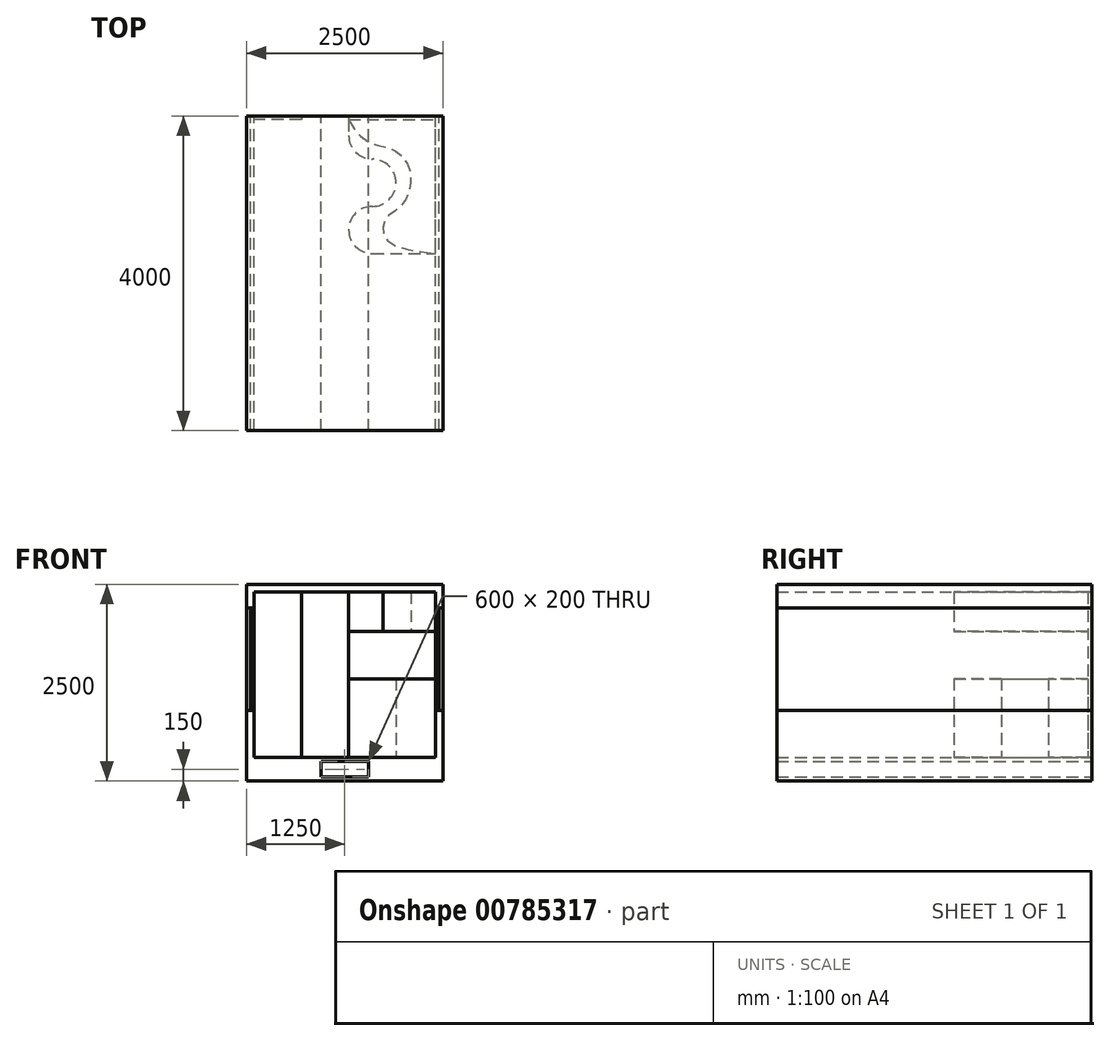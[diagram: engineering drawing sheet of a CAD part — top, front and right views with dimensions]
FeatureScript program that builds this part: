
annotation { "Feature Type Name" : "Feature", "Feature Type Description" : "" }
export const myFeature = defineFeature(function(context is Context, id is Id, definition is map)
    precondition{}
    {
        {
            var Q0;
            Q0=qCreatedBy(makeId("Front.planeOp"),FACE);
            var sketch = newSketch(context, id + "F0", { "sketchPlane" : qUnion([Q0])});
            skLineSegment(sketch, "E0", {"start": v(0, 0) * mm, "end": v(1250, 0) * mm});
            skLineSegment(sketch, "E1", {"start": v(0, 0) * mm, "end": v(-1250, 0) * mm});
            skLineSegment(sketch, "E2", {"start": v(-1250, 0) * mm, "end": v(-1250, 900) * mm});
            skLineSegment(sketch, "E3", {"start": v(-1250, 900) * mm, "end": v(-1150, 900) * mm});
            skLineSegment(sketch, "E4", {"start": v(-1150, 900) * mm, "end": v(-1150, 50) * mm});
            skLineSegment(sketch, "E5", {"start": v(-1150, 50) * mm, "end": v(1150, 50) * mm});
            skLineSegment(sketch, "E6", {"start": v(1150, 50) * mm, "end": v(1150, 900) * mm});
            skLineSegment(sketch, "E7", {"start": v(1150, 900) * mm, "end": v(1250, 900) * mm});
            skLineSegment(sketch, "E8", {"start": v(1250, 900) * mm, "end": v(1250, 0) * mm});
            skLineSegment(sketch, "E9", {"start": v(-1250, 900) * mm, "end": v(-1250, 2200) * mm});
            skLineSegment(sketch, "E10", {"start": v(-1250, 2200) * mm, "end": v(-1250, 2500) * mm});
            skLineSegment(sketch, "E11", {"start": v(-1250, 2500) * mm, "end": v(1250, 2500) * mm});
            skLineSegment(sketch, "E12", {"start": v(1250, 2500) * mm, "end": v(1250, 2200) * mm});
            skLineSegment(sketch, "E13", {"start": v(1250, 2200) * mm, "end": v(1250, 900) * mm});
            skLineSegment(sketch, "E14", {"start": v(-1250, 2200) * mm, "end": v(-1150, 2200) * mm});
            skLineSegment(sketch, "E15", {"start": v(-1150, 2200) * mm, "end": v(-1150, 2400) * mm});
            skLineSegment(sketch, "E16", {"start": v(-1150, 2400) * mm, "end": v(1150, 2400) * mm});
            skLineSegment(sketch, "E17", {"start": v(1150, 2400) * mm, "end": v(1150, 2200) * mm});
            skLineSegment(sketch, "E18", {"start": v(1150, 2200) * mm, "end": v(1250, 2200) * mm});
            skLineSegment(sketch, "E19", {"start": v(-1200, 900) * mm, "end": v(-1200, 2200) * mm});
            skLineSegment(sketch, "E20", {"start": v(1200, 2200) * mm, "end": v(1200, 900) * mm});
            skPoint(sketch, "E21", {"position": v(-1150, 250) * mm});
            skLineSegment(sketch, "E22", {"start": v(-1150, 250) * mm, "end": v(-300, 250) * mm});
            skLineSegment(sketch, "E23", {"start": v(-300, 250) * mm, "end": v(-300, 50) * mm});
            skLineSegment(sketch, "E24", {"start": v(1150, 250) * mm, "end": v(300, 250) * mm});
            skLineSegment(sketch, "E25", {"start": v(300, 250) * mm, "end": v(300, 50) * mm});
            skLineSegment(sketch, "E26", {"start": v(-300, 250) * mm, "end": v(300, 250) * mm});
            skLineSegment(sketch, "E27", {"start": v(-1150, 324) * mm, "end": v(1150, 324) * mm});
            skSolve(sketch);
        }
        {
            var Q0;
            Q0=makeQuery(id+"F0.imprint","IMPRINT",FACE,{"disambiguationData":[TD([[makeQuery(id+"F0.imprint","IMPRINT",EDGE,{"derivedFrom":sQuery(id+"F0.wireOp",EDGE,"E0")}),1.0]])]});
            var Q1;
            {var subQ4=sQuery(id+"F0.wireOp",EDGE,"E24");Q1=makeQuery(id+"F0.imprint","IMPRINT",FACE,{"disambiguationData":[TD([[makeQuery(id+"F0.imprint","IMPRINT",EDGE,{"derivedFrom":subQ4}),1.0]])]});}
            var Q2;
            {var subQ3=sQuery(id+"F0.wireOp",EDGE,"E22");Q2=makeQuery(id+"F0.imprint","IMPRINT",FACE,{"disambiguationData":[TD([[makeQuery(id+"F0.imprint","IMPRINT",EDGE,{"derivedFrom":subQ3}),-1.0]])]});}
            var Q3;
            {var subQ3=sQuery(id+"F0.wireOp",EDGE,"E22");Q3=makeQuery(id+"F0.imprint","IMPRINT",FACE,{"disambiguationData":[TD([[makeQuery(id+"F0.imprint","IMPRINT",EDGE,{"derivedFrom":subQ3}),1.0]])]});}
            var Q4;
            {var subQ1=sQuery(id+"F0.wireOp",EDGE,"E10");Q4=makeQuery(id+"F0.imprint","IMPRINT",FACE,{"disambiguationData":[TD([[makeQuery(id+"F0.imprint","IMPRINT",EDGE,{"derivedFrom":subQ1}),-1.0]])]});}
            extrude(context, id + "F1", {"entities" : qUnion([Q0, Q1, Q2, Q3, Q4]), "depth" : 4000 * mm, "offsetDistance" : 25 * mm});
        }
        {
            var Q0;
            {var subQ0=sQuery(id+"F0.wireOp",EDGE,"E9");Q0=makeQuery(id+"F0.imprint","IMPRINT",FACE,{"disambiguationData":[TD([[makeQuery(id+"F0.imprint","IMPRINT",EDGE,{"derivedFrom":subQ0}),-1.0]])]});}
            var Q1;
            {var subQ0=sQuery(id+"F0.wireOp",EDGE,"E13");Q1=makeQuery(id+"F0.imprint","IMPRINT",FACE,{"disambiguationData":[TD([[makeQuery(id+"F0.imprint","IMPRINT",EDGE,{"derivedFrom":subQ0}),-1.0]])]});}
            extrude(context, id + "F2", {"entities" : qUnion([Q0, Q1]), "depth" : 4000 * mm, "offsetDistance" : 25 * mm});
        }
        {
            var Q0;
            Q0=makeQuery(id+"F1.opExtrude","SWEPT_FACE",FACE,{"disambiguationData":[OSD([sQuery(id+"F0.wireOp",EDGE,"E27")])]});
            extrude(context, id + "F3", {"entities" : qUnion([Q0]), "operationType" : NewBodyOperationType.REMOVE, "oppositeDirection" : true, "depth" : 24 * mm, "offsetDistance" : 25 * mm});
        }
        {
            var Q0;
            Q0=makeQuery(id+"F3.boolean.opBoolean","COPY",FACE,{"derivedFrom":makeQuery(id+"F3.opExtrude","CAP_FACE",FACE,{"disambiguationData":[OSD([sQuery(id+"F0.wireOp",EDGE,"E27")])],"isStart":false})});
            var sketch = newSketch(context, id + "F4", { "sketchPlane" : qUnion([Q0])});
            skLineSegment(sketch, "E28", {"start": v(-1150, 0) * mm, "end": v(-550, 0) * mm});
            skLineSegment(sketch, "E29", {"start": v(-550, 0) * mm, "end": v(-550, -50) * mm});
            skLineSegment(sketch, "E30", {"start": v(-550, -50) * mm, "end": v(-1150, -50) * mm});
            skLineSegment(sketch, "E31", {"start": v(-1150, -50) * mm, "end": v(-1150, 0) * mm});
            skLineSegment(sketch, "E32", {"start": v(50, 0) * mm, "end": v(1150, 0) * mm});
            skLineSegment(sketch, "E33", {"start": v(50, 0) * mm, "end": v(50, -50) * mm});
            skLineSegment(sketch, "E34", {"start": v(50, -50) * mm, "end": v(1150, -50) * mm});
            skLineSegment(sketch, "E35", {"start": v(1150, -50) * mm, "end": v(1150, 0) * mm});
            skSolve(sketch);
        }
        {
            var Q0;
            Q0=makeQuery(id+"F4.imprint","IMPRINT",FACE,{"disambiguationData":[TD([[makeQuery(id+"F4.imprint","IMPRINT",EDGE,{"derivedFrom":sQuery(id+"F4.wireOp",EDGE,"E28")}),-1.0]])]});
            var Q1;
            Q1=makeQuery(id+"F4.imprint","IMPRINT",FACE,{"disambiguationData":[TD([[makeQuery(id+"F4.imprint","IMPRINT",EDGE,{"derivedFrom":sQuery(id+"F4.wireOp",EDGE,"E32")}),-1.0]])]});
            extrude(context, id + "F5", {"entities" : qUnion([Q0, Q1]), "depth" : 2100 * mm, "offsetDistance" : 25 * mm});
        }
        {
            var Q0;
            Q0=makeQuery(id+"F3.boolean.opBoolean","COPY",FACE,{"derivedFrom":makeQuery(id+"F3.opExtrude","CAP_FACE",FACE,{"disambiguationData":[OSD([sQuery(id+"F0.wireOp",EDGE,"E27")])],"isStart":false})});
            var sketch = newSketch(context, id + "F6", { "sketchPlane" : qUnion([Q0])});
            skCircle(sketch, "E36", {"center": v(350, -850) * mm, "radius": 300 * mm});
            skCircle(sketch, "E37", {"center": v(350, -250) * mm, "radius": 300 * mm});
            skCircle(sketch, "E38", {"center": v(350, -1450) * mm, "radius": 300 * mm});
            skLineSegment(sketch, "E39", {"start": v(350, -1750) * mm, "end": v(1150, -1750) * mm});
            skLineSegment(sketch, "E40", {"start": v(1150, -1750) * mm, "end": v(1150, -50) * mm});
            skLineSegment(sketch, "E41", {"start": v(1150, -50) * mm, "end": v(50, -50) * mm});
            skLineSegment(sketch, "E42", {"start": v(50, -50) * mm, "end": v(50, -250) * mm});
            skSolve(sketch);
        }
        {
            var Q0;
            {var subQ0=sQuery(id+"F6.wireOp",EDGE,"E39");Q0=makeQuery(id+"F6.imprint","IMPRINT",FACE,{"disambiguationData":[TD([[makeQuery(id+"F6.imprint","IMPRINT",EDGE,{"derivedFrom":subQ0}),1.0]])]});}
            var Q1;
            {var subQ0=sQuery(id+"F6.wireOp",EDGE,"E38");var subQ1=makeQuery(id+"F6.imprint","INTERSECT",VERTEX,{"derivedFrom":[subQ0,sQuery(id+"F6.wireOp",EDGE,"E39")]});Q1=makeQuery(id+"F6.imprint","IMPRINT",FACE,{"disambiguationData":[TD([[makeQuery(id+"F6.imprint","IMPRINT",EDGE,{"disambiguationData":[TD([[subQ1,1.0]])],"derivedFrom":subQ0}),1.0]])]});}
            var Q2;
            {var subQ0=sQuery(id+"F6.wireOp",EDGE,"E37");var subQ1=makeQuery(id+"F6.imprint","INTERSECT",VERTEX,{"derivedFrom":[subQ0,sQuery(id+"F6.wireOp",EDGE,"E42")]});Q2=makeQuery(id+"F6.imprint","IMPRINT",FACE,{"disambiguationData":[TD([[makeQuery(id+"F6.imprint","IMPRINT",EDGE,{"disambiguationData":[TD([[subQ1,1.0]])],"derivedFrom":subQ0}),1.0]])]});}
            var Q3;
            {var subQ0=sQuery(id+"F6.wireOp",EDGE,"E42");Q3=makeQuery(id+"F6.imprint","IMPRINT",FACE,{"disambiguationData":[TD([[makeQuery(id+"F6.imprint","IMPRINT",EDGE,{"derivedFrom":subQ0}),1.0]])]});}
            extrude(context, id + "F7", {"entities" : qUnion([Q0, Q1, Q2, Q3]), "depth" : 1000 * mm, "offsetDistance" : 25 * mm});
        }
        {
            var Q0;
            Q0=makeQuery(id+"F7.opExtrude","CAP_FACE",FACE,{"disambiguationData":[OSD([sQuery(id+"F6.wireOp",EDGE,"E36"),sQuery(id+"F6.wireOp",EDGE,"E37"),sQuery(id+"F6.wireOp",EDGE,"E38"),sQuery(id+"F6.wireOp",EDGE,"E39"),sQuery(id+"F6.wireOp",EDGE,"E40"),sQuery(id+"F6.wireOp",EDGE,"E41"),sQuery(id+"F6.wireOp",EDGE,"E42")])],"isStart":false});
            var sketch = newSketch(context, id + "F8", { "sketchPlane" : qUnion([Q0])});
            skSolve(sketch);
        }
        {
            var Q0;
            Q0=makeQuery(id+"F8.imprint","IMPRINT",FACE,{"disambiguationData":[TD([[makeQuery(id+"F8.imprint","IMPRINT",EDGE,{"derivedFrom":makeQuery(id+"F7.opExtrude","CAP_EDGE",EDGE,{"disambiguationData":[OSD([sQuery(id+"F6.wireOp",EDGE,"E36")])],"isStart":false})}),-1.0]])]});
            extrude(context, id + "F9", {"entities" : qUnion([Q0]), "depth" : 600 * mm, "offsetDistance" : 25 * mm});
        }
        {
            var Q0;
            Q0=makeQuery(id+"F9.opExtrude","CAP_FACE",FACE,{"disambiguationData":[OSD([sQuery(id+"F6.wireOp",EDGE,"E36"),sQuery(id+"F6.wireOp",EDGE,"E37"),sQuery(id+"F6.wireOp",EDGE,"E38"),sQuery(id+"F6.wireOp",EDGE,"E39"),sQuery(id+"F6.wireOp",EDGE,"E40"),sQuery(id+"F6.wireOp",EDGE,"E41"),sQuery(id+"F6.wireOp",EDGE,"E42")])],"isStart":false});
            var sketch = newSketch(context, id + "F10", { "sketchPlane" : qUnion([Q0])});
            skFitSpline(sketch, "E43", {"points": [v(50, -50) * mm, v(272.37, -318.49) * mm, v(597.06, -421.56) * mm, v(808.37, -632.87) * mm, v(823.83, -936.94) * mm, v(705.3, -1153.4) * mm, v(535.22, -1287.4) * mm, v(483.68, -1436.86) * mm, v(566.14, -1606.94) * mm, v(1150, -1750) * mm], "startDerivative": vector(1556.32, -2623.51) * mm, "endDerivative": vector(4450.45, -562.22) * mm});
            skSolve(sketch);
        }
        {
            var Q0;
            Q0=makeQuery(id+"F10.imprint","IMPRINT",FACE,{"disambiguationData":[TD([[makeQuery(id+"F10.imprint","IMPRINT",EDGE,{"derivedFrom":sQuery(id+"F10.wireOp",EDGE,"E43")}),1.0]])]});
            extrude(context, id + "F11", {"entities" : qUnion([Q0]), "depth" : 500 * mm, "offsetDistance" : 25 * mm});
        }
        {
            var Q0;
            Q0=makeQuery(id+"F9.opExtrude","SWEPT_BODY",BODY,{"disambiguationData":[OSD([sQuery(id+"F6.wireOp",EDGE,"E36"),sQuery(id+"F6.wireOp",EDGE,"E37"),sQuery(id+"F6.wireOp",EDGE,"E38"),sQuery(id+"F6.wireOp",EDGE,"E39"),sQuery(id+"F6.wireOp",EDGE,"E40"),sQuery(id+"F6.wireOp",EDGE,"E41"),sQuery(id+"F6.wireOp",EDGE,"E42")])]});
            deleteBodies(context, id + "F12", {"entities" : qUnion([Q0])});
        }
    });
